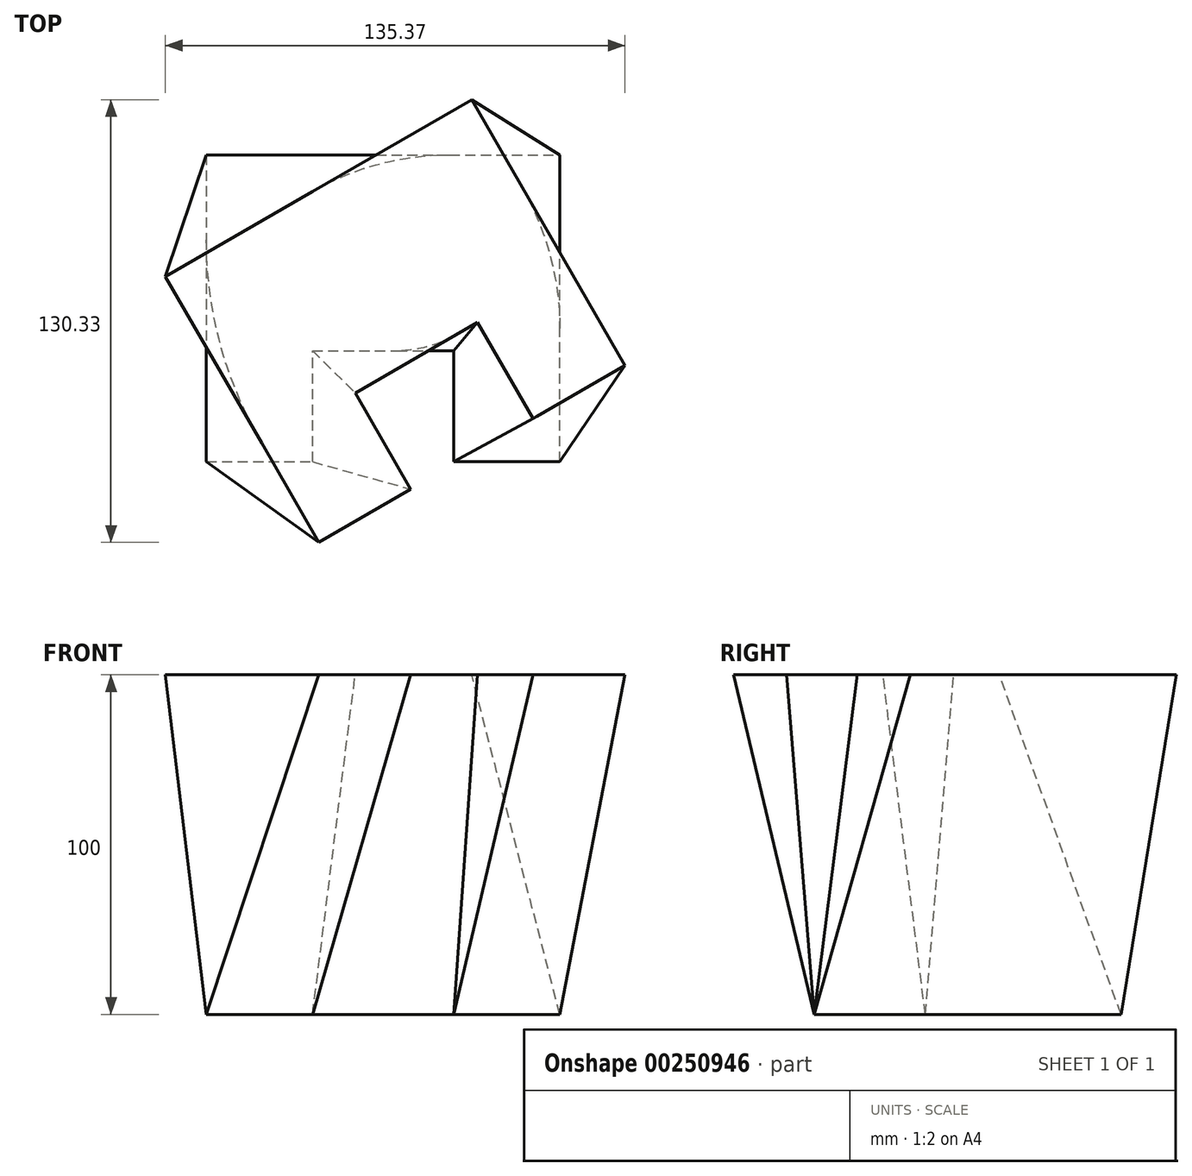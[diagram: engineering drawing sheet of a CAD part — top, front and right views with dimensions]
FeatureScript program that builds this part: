
annotation { "Feature Type Name" : "Feature", "Feature Type Description" : "" }
export const myFeature = defineFeature(function(context is Context, id is Id, definition is map)
    precondition{}
    {
        {
            var Q0;
            Q0=qCreatedBy(makeId("Top.planeOp"),FACE);
            var sketch = newSketch(context, id + "F0", { "sketchPlane" : qUnion([Q0])});
            skLineSegment(sketch, "E0", {"start": v(-55.08, 39.16) * mm, "end": v(-55.08, -51.2) * mm});
            skLineSegment(sketch, "E1", {"start": v(-55.08, -51.2) * mm, "end": v(-23.81, -51.2) * mm});
            skLineSegment(sketch, "E2", {"start": v(-23.81, -51.2) * mm, "end": v(-23.81, -18.5) * mm});
            skLineSegment(sketch, "E3", {"start": v(-23.81, -18.5) * mm, "end": v(17.79, -18.5) * mm});
            skLineSegment(sketch, "E4", {"start": v(17.79, -18.5) * mm, "end": v(17.79, -51.2) * mm});
            skLineSegment(sketch, "E5", {"start": v(17.79, -51.2) * mm, "end": v(49.06, -51.2) * mm});
            skLineSegment(sketch, "E6", {"start": v(49.06, -51.2) * mm, "end": v(49.06, 40.02) * mm});
            skLineSegment(sketch, "E7", {"start": v(-55.08, 39.16) * mm, "end": v(49.06, 39.16) * mm});
            skPoint(sketch, "E8", {"position": v(0, 0) * mm});
            skSolve(sketch);
        }
        {
            var Q0;
            Q0=qCreatedBy(makeId("Top.planeOp"),FACE);
            cPlane(context, id + "F1", {"entities" : qUnion([Q0]), "cplaneType" : CPlaneType.OFFSET, "offset" : 100 * mm, "width" : 150 * mm, "height" : 150 * mm});
        }
        {
            var Q0;
            Q0=qCreatedBy(id+"F1.planeOp",FACE);
            var sketch = newSketch(context, id + "F2", { "sketchPlane" : qUnion([Q0])});
            skLineSegment(sketch, "E9", {"start": v(-67.13, 3.33) * mm, "end": v(-21.95, -74.93) * mm});
            skLineSegment(sketch, "E10", {"start": v(-21.95, -74.93) * mm, "end": v(5.14, -59.3) * mm});
            skLineSegment(sketch, "E11", {"start": v(5.14, -59.3) * mm, "end": v(-11.22, -30.97) * mm});
            skLineSegment(sketch, "E12", {"start": v(-11.22, -30.97) * mm, "end": v(24.8, -10.17) * mm});
            skLineSegment(sketch, "E13", {"start": v(24.8, -10.17) * mm, "end": v(41.16, -38.5) * mm});
            skLineSegment(sketch, "E14", {"start": v(41.16, -38.5) * mm, "end": v(68.24, -22.86) * mm});
            skLineSegment(sketch, "E15", {"start": v(68.24, -22.86) * mm, "end": v(22.63, 56.15) * mm});
            skLineSegment(sketch, "E16", {"start": v(-67.13, 3.33) * mm, "end": v(23.06, 55.4) * mm});
            skPoint(sketch, "E17", {"position": v(0.15, -3.04) * mm});
            skLineSegment(sketch, "E18.0", {"start": v(-21.95, -74.93) * mm, "end": v(41.16, -38.5) * mm, "construction": true});
            skLineSegment(sketch, "E19.0", {"start": v(23.06, 55.4) * mm, "end": v(22.63, 56.15) * mm, "construction": true});
            skSolve(sketch);
        }
        {
            var Q0;
            Q0=makeQuery(id+"F0.imprint","IMPRINT",FACE,{"disambiguationData":[TD([[makeQuery(id+"F0.imprint","IMPRINT",EDGE,{"derivedFrom":sQuery(id+"F0.wireOp",EDGE,"E0")}),1.0]])]});
            var Q1;
            Q1=makeQuery(id+"F2.imprint","IMPRINT",FACE,{"disambiguationData":[TD([[makeQuery(id+"F2.imprint","IMPRINT",EDGE,{"derivedFrom":sQuery(id+"F2.wireOp",EDGE,"E9")}),1.0]])]});
            loft(context, id + "F3", {"sheetProfilesArray" : [{ "sheetProfileEntities" : qUnion([Q0]) }, { "sheetProfileEntities" : qUnion([Q1]) }]});
        }
    });
